# Revit family: NBS_HeatraeSadia_StrgWtrHtrsElctrc_Streamline_Oversink
name_source: partatom
category: Plumbing Fixtures
revit_build: Autodesk Revit 2014 (Build: 20130709_2115(x64)
units: mm (PartAtom-declared; Revit-internal decimal feet)

## types (4) — shared parameters
Accessories = Telescopic spout (95:970:513)
Arrangement = Single point – mains supply
AssetType = Fixed
BodyHeight = 475 mm  [stored 1.5584 ft]
CW Connection = Yes
CasingFinish = White thermoplastic
Color = White
Connections = Supplied direct from rising main or cistern (minimum head of 4 m) using 15 mm O/D pipe
Controls = Control knob
Description = Vented point of use storage water heater
DurationUnit = year
Features = Compact, low profile, anti-frost protection
Fixing = Wall fixed oversink
FlowRate = To suit draw off requirements
HW Connection = No
HeatTransferSurfaceArea = 0
Height = 500 mm  [stored 1.64042 ft]
IPCode = IPX4
IfcExportAs = IfcBoilerType
IfcExportType = WATER
IsWaterStorageHeater = Yes
ManufacturerName = Heatrae Sadia
ManufacturerURL = www.heatraesadia.com
Material = Outer casing: Moulded thermoplastic; Water container: Polypropylene; Heat unit: Rod-type element sheathed in corrosion resistant alloy
NBSCertification = http://www.nationalbimlibrary.com
NBSDescription = Storage water heaters, electric
NBSReference = 90-15-35/440
NominalHeight = 500 mm  [stored 1.64042 ft]
NominalWidth = 290 mm  [stored 0.951444 ft]
OutletTemperatureRange = 5, 70
PartialLoadEfficiencyCurves = 0
PressureRating = 0
ProductInformation = www.heatraesadia.com/docs/344_084_POU-Vented_lit-AW_online.pdf
SafetyFeatures = Dry start cut-out, frost protection thermostat setting, thermostat setting lockable at 40°C for hand washing
SpoutProjection = 346 mm
StorageWaterHeaterMaterial = NBS_Concept
ThermalInsulation = CFC/HCFC free (ODP zero) flame-retardant expanded polyurethane
ThirdPartyCertification = Nemko approved
Uniclass2 = 90-90-46/428
Uniclass2015Description = Electric storage water heaters
Uniclass2015Reference = Pr_60_60_96_28
Uniclass2015Version = Products v1.1
Vent Connection = No
Version = 1
WarrantyDurationParts = 2
WarrantyDurationUnit = year
WarrantyStartDate = 1900-12-31T23:59:59
Waste Connection = No
WaterInletTemperatureRange = 0
Width = 290 mm  [stored 0.951444 ft]
zero-valued in all types: HeatOutput, NominalEfficiency, NominalEnergyConsumption, NominalPartLoadRatio

## per-type parameters (varying)
| type | BIMObjectName | Depth | ModelNumber | ModelReference | Name | NominalLength | Rating | Size | WaterStorageCapacity | Weight |
| 7-1kW | NBS_HeatraeSadia_StorageWaterHeatersElectric_StreamlineOversink_7-1kW | 178 mm  [stored 0.58399 ft] | 95:010:281 | Streamline 7 1kW oversink | StorageWaterHeatersElectric_StreamlineOversink_7-1kW_HeatraeSadia | 178 mm  [stored 0.58399 ft] | 1.0 kW | 500 x 290 x 178 mm | 7 | 10.6 |
| 7-3kW | NBS_HeatraeSadia_StorageWaterHeatersElectric_StreamlineOversink_7-3kW | 178 mm  [stored 0.58399 ft] | 95:010:283 | Streamline 7 3kW oversink | StorageWaterHeatersElectric_StreamlineOversink_7-3kW_HeatraeSadia | 178 mm  [stored 0.58399 ft] | 3.0 kW | 500 x 290 x 178 mm | 7 | 10.6 |
| 10-1kW | NBS_HeatraeSadia_StorageWaterHeatersElectric_StreamlineOversink_10-1kW | 278 mm  [stored 0.912073 ft] | 95:010:285 | Streamline 10 1kW oversink | StorageWaterHeatersElectric_StreamlineOversink_10-1kW_HeatraeSadia | 278 mm  [stored 0.912073 ft] | 1.0 kW | 500 x 290 x 278 mm | 10 | 14 |
| 10-3kW | NBS_HeatraeSadia_StorageWaterHeatersElectric_StreamlineOversink_10-3kW | 278 mm  [stored 0.912073 ft] | 95:010:287 | Streamline 10 3kW oversink | StorageWaterHeatersElectric_StreamlineOversink_10-3kW_HeatraeSadia | 278 mm  [stored 0.912073 ft] | 3.0 kW | 500 x 290 x 278 mm | 10 | 14 |

note: [stored X ft] marks values corroborated as IEEE doubles in the binary element streams (Revit-internal decimal feet)

## geometry (parser evidence)
native form markers: Blend x13
no freeform markers — native parametric forms only
